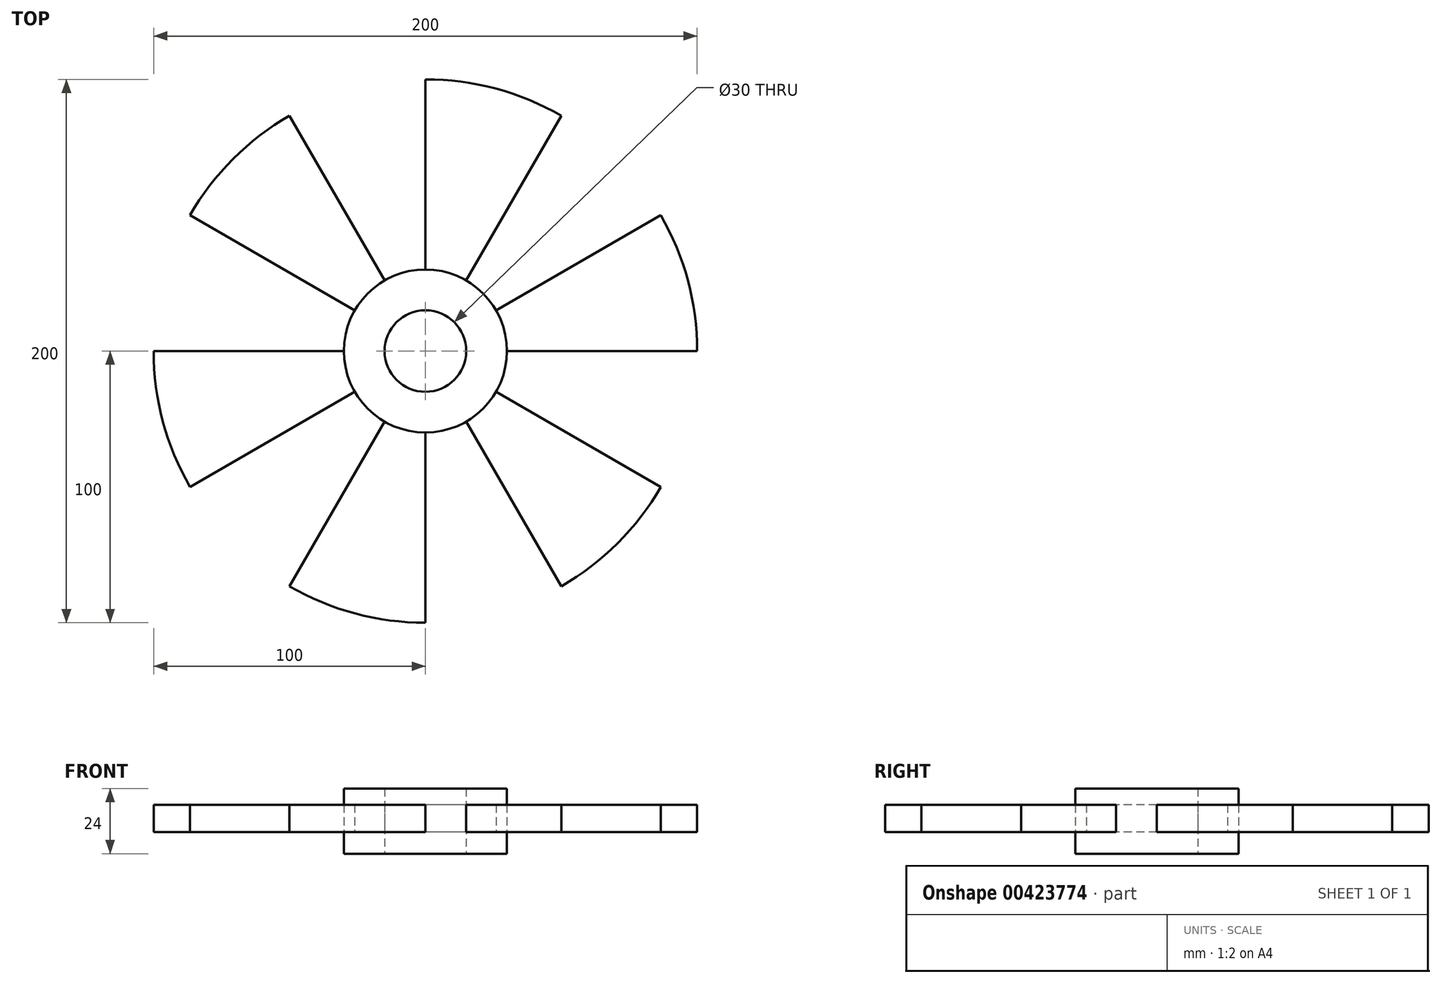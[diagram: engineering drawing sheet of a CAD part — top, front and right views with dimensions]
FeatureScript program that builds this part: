
annotation { "Feature Type Name" : "Feature", "Feature Type Description" : "" }
export const myFeature = defineFeature(function(context is Context, id is Id, definition is map)
    precondition{}
    {
        {
            var Q0;
            Q0=qCreatedBy(makeId("Top.planeOp"),FACE);
            var sketch = newSketch(context, id + "F0", { "sketchPlane" : qUnion([Q0])});
            skCircle(sketch, "E0", {"center": v(0, 0) * mm, "radius": 15 * mm});
            skCircle(sketch, "E1", {"center": v(0, 0) * mm, "radius": 30 * mm});
            skSolve(sketch);
        }
        {
            var Q0;
            Q0 = qSketchRegion(id + "F0", true);
            extrude(context, id + "F1", {"entities" : qUnion([Q0]), "depth" : 16 * mm, "hasSecondDirection" : true, "secondDirectionOppositeDirection" : true, "secondDirectionDepth" : 8 * mm});
        }
        {
            var Q0;
            Q0=qCreatedBy(makeId("Top.planeOp"),FACE);
            var sketch = newSketch(context, id + "F2", { "sketchPlane" : qUnion([Q0])});
            skArc(sketch, "E2", {"start": v(50, 86.6) * mm, "mid": v(25.88, 96.6) * mm, "end": v(0, 100) * mm});
            skLineSegment(sketch, "E3", {"start": v(0, 30) * mm, "end": v(0, 100) * mm});
            skLineSegment(sketch, "E4", {"start": v(15, 25.98) * mm, "end": v(50, 86.6) * mm});
            skArc(sketch, "E5.0", {"start": v(15, 25.98) * mm, "mid": v(7.76, 28.98) * mm, "end": v(0, 30) * mm});
            skSolve(sketch);
        }
        {
            var Q0;
            Q0 = qSketchRegion(id + "F2", true);
            extrude(context, id + "F3", {"entities" : qUnion([Q0]), "depth" : 10 * mm});
        }
        {
            var Q0;
            Q0=qCreatedBy(makeId("Right.planeOp"),FACE);
            var sketch = newSketch(context, id + "F4", { "sketchPlane" : qUnion([Q0])});
            skLineSegment(sketch, "E6", {"start": v(0, 58.63) * mm, "end": v(0, -46.2) * mm, "construction": true});
            skSolve(sketch);
        }
        {
            var Q0;
            Q0=makeQuery(id+"F3.opExtrude","SWEPT_BODY",BODY,{"disambiguationData":[OSD([sQuery(id+"F2.wireOp",EDGE,"E2"),sQuery(id+"F2.wireOp",EDGE,"E3"),sQuery(id+"F2.wireOp",EDGE,"E4"),sQuery(id+"F2.wireOp",EDGE,"E5.0")])]});
            var Q1;
            Q1=sQuery(id+"F4.wireOp",EDGE,"E6");
            circularPattern(context, id + "F5", {"entities" : qUnion([Q0]), "axis" : qUnion([Q1]), "angle" : 360 * degree, "instanceCount" : 6, "equalSpace" : true});
        }
    });
